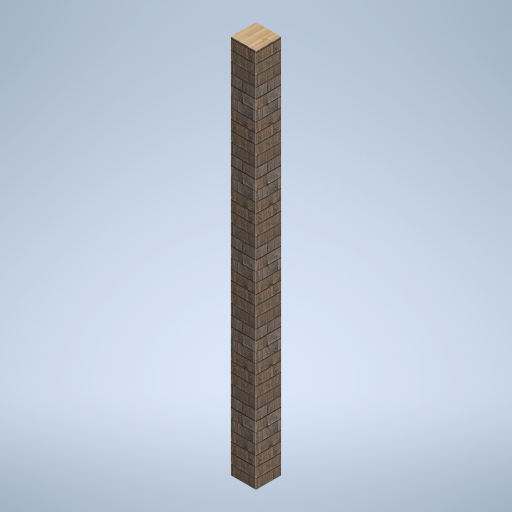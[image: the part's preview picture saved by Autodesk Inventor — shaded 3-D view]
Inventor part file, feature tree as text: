
AUTODESK INVENTOR PART (.ipt)
format: ipt  version: 2024.2 (Build 282272000, 272)  size: 312,832 bytes
history: native  units: in
note: dims shown in document units (in); Inventor stores cm internally (conversion verified against a paired STEP export)
features: other x3, sketch x1
ambient origin geometry x8: Origin, YZ Plane, XZ Plane, XY Plane, X Axis, Y Axis, Z Axis, Center Point
bodies: Solid1 (feature_tree)
feature tree (4):
  other  "support_frame_03.ipt"
  other  "Solid1::support_frame_03.ipt"
  other  "TaggingFeature1"
  sketch  "Sketch1"  dims[d0=0.3937in]
